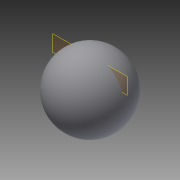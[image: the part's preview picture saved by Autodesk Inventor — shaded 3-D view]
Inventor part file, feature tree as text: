
AUTODESK INVENTOR PART (.ipt)
format: ipt  version: 2013 (Build 170138000, 138)  size: 103,424 bytes
history: native  units: in
note: dims shown in document units (in); Inventor stores cm internally (conversion verified against a paired STEP export)
features: plane x1, revolve x1, sketch x1
ambient origin geometry x8: Origin, YZ Plane, XZ Plane, XY Plane, X Axis, Y Axis, Z Axis, Center Point
bodies: Solid1 (feature_tree)
feature tree (3):
  plane  "Work Plane1"
  revolve  "Revolution1"  [1 undecoded]
  sketch  "Sketch1"  dims[d0=4.5in d1=12.0in d2=0.0in d3=24.0in d4=90.0deg]
note: 1 required parameter value undecoded (feature->parameter linkage not recoverable at this tier; creation-order binding heuristic only, values carry confidence <= 0.55)
